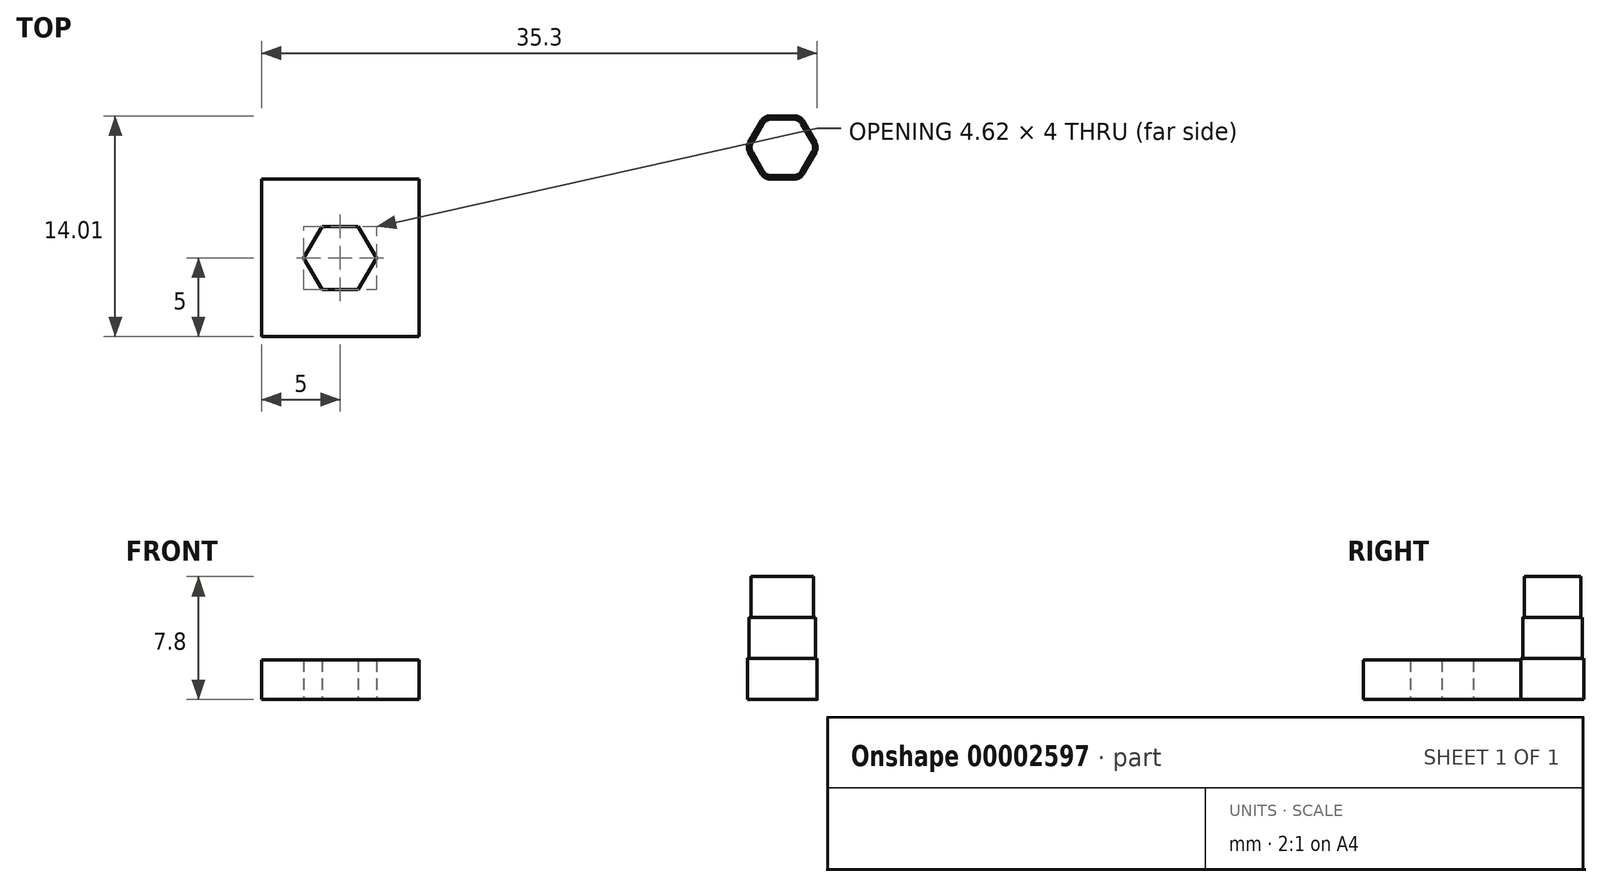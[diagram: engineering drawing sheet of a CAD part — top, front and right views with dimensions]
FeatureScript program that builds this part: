
annotation { "Feature Type Name" : "Feature", "Feature Type Description" : "" }
export const myFeature = defineFeature(function(context is Context, id is Id, definition is map)
    precondition{}
    {
        {
            var Q0;
            Q0=qCreatedBy(makeId("Top.planeOp"),FACE);
            var sketch = newSketch(context, id + "F0", { "sketchPlane" : qUnion([Q0])});
            skLineSegment(sketch, "E0.rect.bottom", {"start": v(-5, 5) * mm, "end": v(5, 5) * mm});
            skLineSegment(sketch, "E0.rect.top", {"start": v(-5, -5) * mm, "end": v(5, -5) * mm});
            skLineSegment(sketch, "E0.rect.left", {"start": v(-5, 5) * mm, "end": v(-5, -5) * mm});
            skLineSegment(sketch, "E0.rect.right", {"start": v(5, 5) * mm, "end": v(5, -5) * mm});
            skPoint(sketch, "E0.rect.middle", {"position": v(0, 0) * mm});
            skCircle(sketch, "E1.cCircle", {"center": v(0, 0) * mm, "radius": 2 * mm, "construction": true});
            skLineSegment(sketch, "E1.0", {"start": v(1.15, -2) * mm, "end": v(-1.15, -2) * mm});
            skLineSegment(sketch, "E1.1", {"start": v(-1.15, -2) * mm, "end": v(-2.3, 0) * mm});
            skLineSegment(sketch, "E1.2", {"start": v(-2.3, 0) * mm, "end": v(-1.15, 2) * mm});
            skLineSegment(sketch, "E1.3", {"start": v(-1.15, 2) * mm, "end": v(1.15, 2) * mm});
            skLineSegment(sketch, "E1.4", {"start": v(1.15, 2) * mm, "end": v(2.3, 0) * mm});
            skLineSegment(sketch, "E1.5", {"start": v(2.3, 0) * mm, "end": v(1.15, -2) * mm});
            skPoint(sketch, "E1.0.midPoint", {"position": v(0, -2) * mm});
            skLineSegment(sketch, "E2", {"start": v(-2.3, 0) * mm, "end": v(2.3, 0) * mm, "construction": true});
            skCircle(sketch, "E3.cCircle", {"center": v(28.09, 7.01) * mm, "radius": 2 * mm, "construction": true});
            skLineSegment(sketch, "E3.0", {"start": v(30.4, 7.01) * mm, "end": v(29.24, 5.01) * mm});
            skLineSegment(sketch, "E3.1", {"start": v(29.24, 5.01) * mm, "end": v(26.93, 5.01) * mm});
            skLineSegment(sketch, "E3.2", {"start": v(26.93, 5.01) * mm, "end": v(25.78, 7.01) * mm});
            skLineSegment(sketch, "E3.3", {"start": v(25.78, 7.01) * mm, "end": v(26.93, 9.01) * mm});
            skLineSegment(sketch, "E3.4", {"start": v(26.93, 9.01) * mm, "end": v(29.24, 9.01) * mm});
            skLineSegment(sketch, "E3.5", {"start": v(29.24, 9.01) * mm, "end": v(30.4, 7.01) * mm});
            skPoint(sketch, "E3.0.midPoint", {"position": v(29.82, 6.01) * mm});
            skSolve(sketch);
        }
        {
            var Q0;
            Q0=makeQuery(id+"F0.imprint","IMPRINT",FACE,{"disambiguationData":[TD([[makeQuery(id+"F0.imprint","IMPRINT",EDGE,{"derivedFrom":sQuery(id+"F0.wireOp",EDGE,"E0.rect.bottom")}),-1.0]])]});
            extrude(context, id + "F1", {"entities" : qUnion([Q0]), "depth" : 2.5 * mm});
        }
        {
            var Q0;
            Q0=makeQuery(id+"F0.imprint","IMPRINT",FACE,{"disambiguationData":[TD([[makeQuery(id+"F0.imprint","IMPRINT",EDGE,{"derivedFrom":sQuery(id+"F0.wireOp",EDGE,"E3.0")}),-1.0]])]});
            extrude(context, id + "F2", {"entities" : qUnion([Q0]), "depth" : 2.6 * mm});
        }
        {
            var Q0;
            Q0=makeQuery(id+"F2.opExtrude","CAP_FACE",FACE,{"disambiguationData":[OSD([sQuery(id+"F0.wireOp",EDGE,"E3.0"),sQuery(id+"F0.wireOp",EDGE,"E3.1"),sQuery(id+"F0.wireOp",EDGE,"E3.2"),sQuery(id+"F0.wireOp",EDGE,"E3.3"),sQuery(id+"F0.wireOp",EDGE,"E3.4"),sQuery(id+"F0.wireOp",EDGE,"E3.5")])],"isStart":false});
            var sketch = newSketch(context, id + "F3", { "sketchPlane" : qUnion([Q0])});
            skLineSegment(sketch, "E4.0", {"start": v(26.93, 9.01) * mm, "end": v(29.24, 9.01) * mm});
            skLineSegment(sketch, "E5.0", {"start": v(25.78, 7.01) * mm, "end": v(26.93, 9.01) * mm});
            skPoint(sketch, "E6.0", {"position": v(28.09, 7.01) * mm});
            skCircle(sketch, "E7.cCircle", {"center": v(28.09, 7.01) * mm, "radius": 1.9 * mm, "construction": true});
            skLineSegment(sketch, "E7.0", {"start": v(29.18, 5.11) * mm, "end": v(26.99, 5.11) * mm});
            skLineSegment(sketch, "E7.1", {"start": v(26.99, 5.11) * mm, "end": v(25.9, 7.01) * mm});
            skLineSegment(sketch, "E7.2", {"start": v(25.9, 7.01) * mm, "end": v(26.99, 8.91) * mm});
            skLineSegment(sketch, "E7.3", {"start": v(26.99, 8.91) * mm, "end": v(29.18, 8.91) * mm});
            skLineSegment(sketch, "E7.4", {"start": v(29.18, 8.91) * mm, "end": v(30.28, 7.01) * mm});
            skLineSegment(sketch, "E7.5", {"start": v(30.28, 7.01) * mm, "end": v(29.18, 5.11) * mm});
            skPoint(sketch, "E7.0.midPoint", {"position": v(28.09, 5.11) * mm});
            skSolve(sketch);
        }
        {
            var Q0;
            Q0 = qSketchRegion(id + "F3", true);
            extrude(context, id + "F4", {"entities" : qUnion([Q0]), "operationType" : NewBodyOperationType.ADD, "depth" : 2.6 * mm});
        }
        {
            var Q0;
            Q0=makeQuery(id+"F4.opExtrude","CAP_FACE",FACE,{"disambiguationData":[OSD([sQuery(id+"F3.wireOp",EDGE,"E7.0"),sQuery(id+"F3.wireOp",EDGE,"E7.1"),sQuery(id+"F3.wireOp",EDGE,"E7.2"),sQuery(id+"F3.wireOp",EDGE,"E7.3"),sQuery(id+"F3.wireOp",EDGE,"E7.4"),sQuery(id+"F3.wireOp",EDGE,"E7.5")])],"isStart":false});
            var sketch = newSketch(context, id + "F5", { "sketchPlane" : qUnion([Q0])});
            skPoint(sketch, "E8.0", {"position": v(28.09, 7.01) * mm});
            skCircle(sketch, "E9.cCircle", {"center": v(28.09, 7.01) * mm, "radius": 1.8 * mm, "construction": true});
            skLineSegment(sketch, "E9.0", {"start": v(29.13, 5.21) * mm, "end": v(27.05, 5.21) * mm});
            skLineSegment(sketch, "E9.1", {"start": v(27.05, 5.21) * mm, "end": v(26, 7.01) * mm});
            skLineSegment(sketch, "E9.2", {"start": v(26, 7.01) * mm, "end": v(27.05, 8.81) * mm});
            skLineSegment(sketch, "E9.3", {"start": v(27.05, 8.81) * mm, "end": v(29.13, 8.81) * mm});
            skLineSegment(sketch, "E9.4", {"start": v(29.13, 8.81) * mm, "end": v(30.16, 7.01) * mm});
            skLineSegment(sketch, "E9.5", {"start": v(30.16, 7.01) * mm, "end": v(29.13, 5.21) * mm});
            skPoint(sketch, "E9.0.midPoint", {"position": v(28.09, 5.21) * mm});
            skSolve(sketch);
        }
        {
            var Q0;
            Q0=makeQuery(id+"F5.imprint","IMPRINT",FACE,{"disambiguationData":[TD([[makeQuery(id+"F5.imprint","IMPRINT",EDGE,{"derivedFrom":sQuery(id+"F5.wireOp",EDGE,"E9.0")}),-1.0]])]});
            extrude(context, id + "F6", {"entities" : qUnion([Q0]), "operationType" : NewBodyOperationType.ADD, "depth" : 2.6 * mm});
        }
        {
            var Q0;
            Q0=makeQuery(id+"F4.opExtrude","SWEPT_EDGE",EDGE,{"disambiguationData":[OSD([sQuery(id+"F3.wireOp",EDGE,"E7.0"),sQuery(id+"F3.wireOp",EDGE,"E7.1")])]});
            var Q1;
            Q1=makeQuery(id+"F6.opExtrude","SWEPT_EDGE",EDGE,{"disambiguationData":[OSD([sQuery(id+"F5.wireOp",EDGE,"E9.0"),sQuery(id+"F5.wireOp",EDGE,"E9.1")])]});
            var Q2;
            Q2=makeQuery(id+"F2.opExtrude","SWEPT_EDGE",EDGE,{"disambiguationData":[OSD([sQuery(id+"F0.wireOp",EDGE,"E3.1"),sQuery(id+"F0.wireOp",EDGE,"E3.2")])]});
            var Q3;
            Q3=makeQuery(id+"F2.opExtrude","SWEPT_EDGE",EDGE,{"disambiguationData":[OSD([sQuery(id+"F0.wireOp",EDGE,"E3.2"),sQuery(id+"F0.wireOp",EDGE,"E3.3")])]});
            var Q4;
            Q4=makeQuery(id+"F4.opExtrude","SWEPT_EDGE",EDGE,{"disambiguationData":[OSD([sQuery(id+"F3.wireOp",EDGE,"E7.1"),sQuery(id+"F3.wireOp",EDGE,"E7.2")])]});
            var Q5;
            Q5=makeQuery(id+"F6.opExtrude","SWEPT_EDGE",EDGE,{"disambiguationData":[OSD([sQuery(id+"F5.wireOp",EDGE,"E9.1"),sQuery(id+"F5.wireOp",EDGE,"E9.2")])]});
            var Q6;
            Q6=makeQuery(id+"F6.opExtrude","SWEPT_EDGE",EDGE,{"disambiguationData":[OSD([sQuery(id+"F5.wireOp",EDGE,"E9.0"),sQuery(id+"F5.wireOp",EDGE,"E9.5")])]});
            var Q7;
            Q7=makeQuery(id+"F4.opExtrude","SWEPT_EDGE",EDGE,{"disambiguationData":[OSD([sQuery(id+"F3.wireOp",EDGE,"E7.0"),sQuery(id+"F3.wireOp",EDGE,"E7.5")])]});
            var Q8;
            Q8=makeQuery(id+"F2.opExtrude","SWEPT_EDGE",EDGE,{"disambiguationData":[OSD([sQuery(id+"F0.wireOp",EDGE,"E3.0"),sQuery(id+"F0.wireOp",EDGE,"E3.1")])]});
            var Q9;
            Q9=makeQuery(id+"F2.opExtrude","SWEPT_EDGE",EDGE,{"disambiguationData":[OSD([sQuery(id+"F0.wireOp",EDGE,"E3.0"),sQuery(id+"F0.wireOp",EDGE,"E3.5")])]});
            var Q10;
            Q10=makeQuery(id+"F4.opExtrude","SWEPT_EDGE",EDGE,{"disambiguationData":[OSD([sQuery(id+"F3.wireOp",EDGE,"E7.4"),sQuery(id+"F3.wireOp",EDGE,"E7.5")])]});
            var Q11;
            Q11=makeQuery(id+"F6.opExtrude","SWEPT_EDGE",EDGE,{"disambiguationData":[OSD([sQuery(id+"F5.wireOp",EDGE,"E9.4"),sQuery(id+"F5.wireOp",EDGE,"E9.5")])]});
            var Q12;
            Q12=makeQuery(id+"F6.opExtrude","SWEPT_EDGE",EDGE,{"disambiguationData":[OSD([sQuery(id+"F5.wireOp",EDGE,"E9.3"),sQuery(id+"F5.wireOp",EDGE,"E9.4")])]});
            var Q13;
            Q13=makeQuery(id+"F4.opExtrude","SWEPT_EDGE",EDGE,{"disambiguationData":[OSD([sQuery(id+"F3.wireOp",EDGE,"E7.3"),sQuery(id+"F3.wireOp",EDGE,"E7.4")])]});
            var Q14;
            Q14=makeQuery(id+"F2.opExtrude","SWEPT_EDGE",EDGE,{"disambiguationData":[OSD([sQuery(id+"F0.wireOp",EDGE,"E3.4"),sQuery(id+"F0.wireOp",EDGE,"E3.5")])]});
            var Q15;
            Q15=makeQuery(id+"F2.opExtrude","SWEPT_EDGE",EDGE,{"disambiguationData":[OSD([sQuery(id+"F0.wireOp",EDGE,"E3.3"),sQuery(id+"F0.wireOp",EDGE,"E3.4")])]});
            var Q16;
            Q16=makeQuery(id+"F4.opExtrude","SWEPT_EDGE",EDGE,{"disambiguationData":[OSD([sQuery(id+"F3.wireOp",EDGE,"E7.2"),sQuery(id+"F3.wireOp",EDGE,"E7.3")])]});
            var Q17;
            Q17=makeQuery(id+"F6.opExtrude","SWEPT_EDGE",EDGE,{"disambiguationData":[OSD([sQuery(id+"F5.wireOp",EDGE,"E9.2"),sQuery(id+"F5.wireOp",EDGE,"E9.3")])]});
            fillet(context, id + "F7", {"entities" : qUnion([Q0, Q1, Q2, Q3, Q4, Q5, Q6, Q7, Q8, Q9, Q10, Q11, Q12, Q13, Q14, Q15, Q16, Q17]), "radius" : 0.6 * mm, "tangentPropagation" : true, "allowEdgeOverflow" : false});
        }
    });
